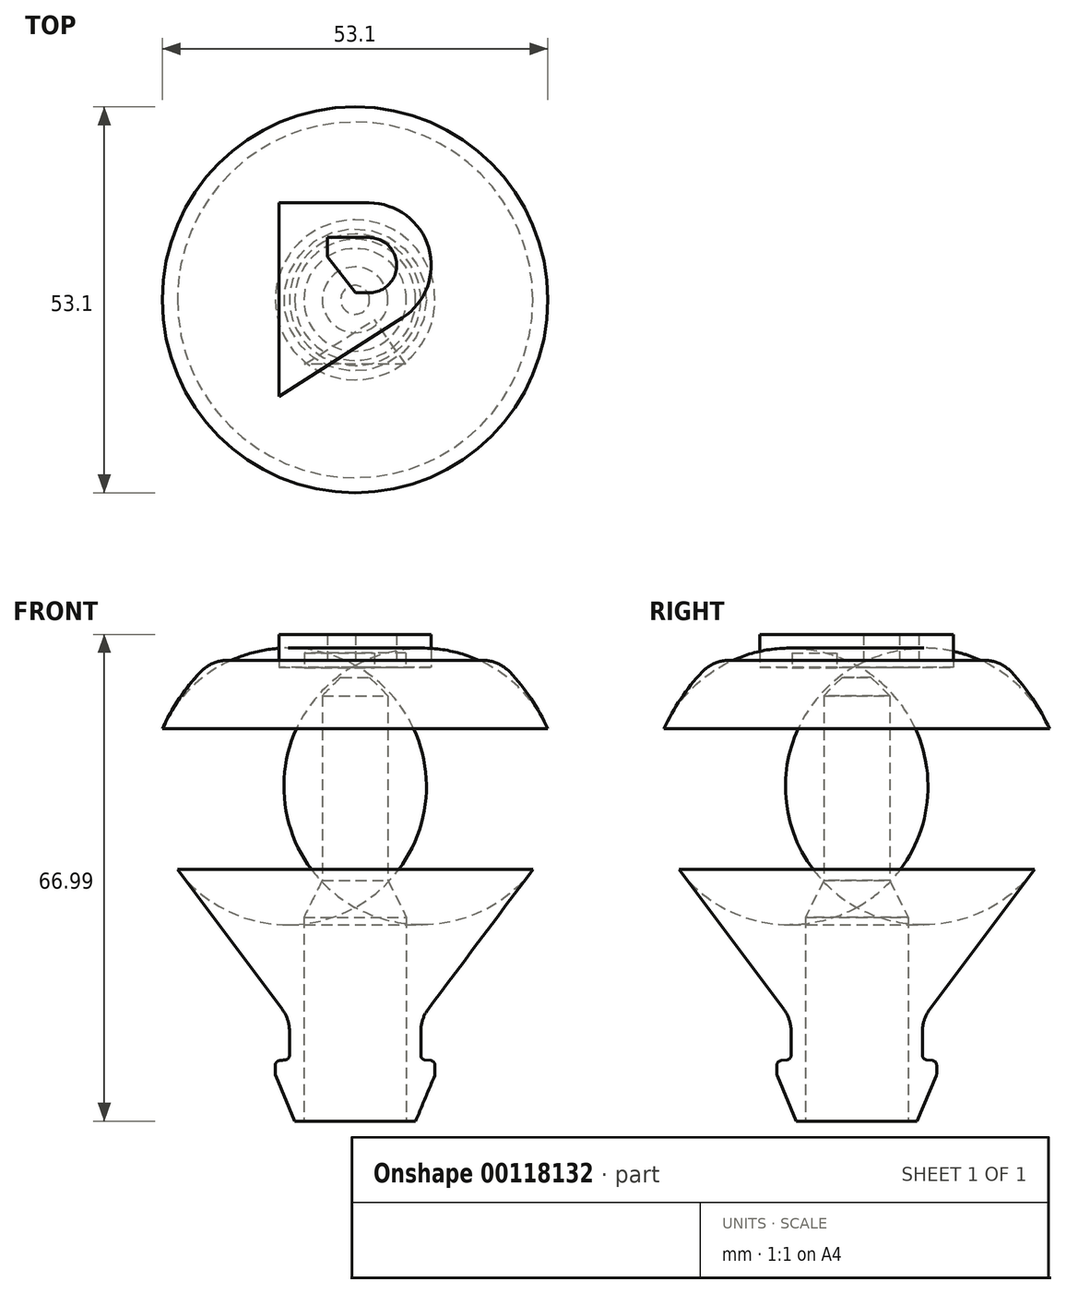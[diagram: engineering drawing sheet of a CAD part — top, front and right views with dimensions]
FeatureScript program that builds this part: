
annotation { "Feature Type Name" : "Feature", "Feature Type Description" : "" }
export const myFeature = defineFeature(function(context is Context, id is Id, definition is map)
    precondition{}
    {
        {
            var Q0;
            Q0=qCreatedBy(makeId("Front.planeOp"),FACE);
            var sketch = newSketch(context, id + "F0", { "sketchPlane" : qUnion([Q0])});
            skLineSegment(sketch, "E0", {"start": v(11, 6.35) * mm, "end": v(8.33, 0) * mm});
            skLineSegment(sketch, "E1", {"start": v(11, 6.35) * mm, "end": v(11, 8.26) * mm});
            skLineSegment(sketch, "E2", {"start": v(9.04, 8.5) * mm, "end": v(11, 8.26) * mm});
            skLineSegment(sketch, "E3", {"start": v(9.04, 8.5) * mm, "end": v(9.04, 14.05) * mm});
            skPoint(sketch, "E4", {"position": v(0, 61.09) * mm});
            skPoint(sketch, "E5", {"position": v(0, 75.49) * mm});
            skArc(sketch, "E6", {"start": v(29.2, 40.92) * mm, "mid": v(26.9, 53.2) * mm, "end": v(19.67, 63.41) * mm});
            skLineSegment(sketch, "E7", {"start": v(8.33, 0) * mm, "end": v(0, 0) * mm});
            skPoint(sketch, "E8", {"position": v(0, 71.03) * mm});
            skPoint(sketch, "E9", {"position": v(7.06, 0) * mm});
            skLineSegment(sketch, "E10", {"start": v(7.06, 0) * mm, "end": v(7.06, 28.07) * mm});
            skLineSegment(sketch, "E11", {"start": v(1.98, 61.09) * mm, "end": v(0, 61.09) * mm});
            skLineSegment(sketch, "E12", {"start": v(0, 61.09) * mm, "end": v(0, 63.41) * mm});
            skLineSegment(sketch, "E13", {"start": v(0, 63.41) * mm, "end": v(19.67, 63.41) * mm});
            skLineSegment(sketch, "E14", {"start": v(9.04, 14.05) * mm, "end": v(31.9, 44.53) * mm});
            skLineSegment(sketch, "E15", {"start": v(4.52, 58.55) * mm, "end": v(4.52, 33.15) * mm});
            skLineSegment(sketch, "E16", {"start": v(1.98, 61.09) * mm, "end": v(4.52, 58.55) * mm});
            skLineSegment(sketch, "E17", {"start": v(4.52, 33.15) * mm, "end": v(7.06, 28.07) * mm});
            skPoint(sketch, "E18.orphan", {"position": v(7.06, 61.09) * mm});
            skSolve(sketch);
        }
        {
            var Q0;
            {var subQ0=sQuery(id+"F0.wireOp",EDGE,"E0");Q0=makeQuery(id+"F0.imprint","IMPRINT",FACE,{"disambiguationData":[TD([[makeQuery(id+"F0.imprint","IMPRINT",EDGE,{"derivedFrom":subQ0}),-1.0]])]});}
            var Q1;
            Q1=sQuery(id+"F0.wireOp",EDGE,"E12");
            revolve(context, id + "F1", {"entities" : qUnion([Q0]), "axis" : qUnion([Q1]), "revolveType" : RevolveType.FULL});
        }
        {
            var Q0;
            Q0=makeQuery(id+"F1.opRevolve","SWEPT_EDGE",EDGE,{"disambiguationData":[OSD([sQuery(id+"F0.wireOp",EDGE,"E6"),sQuery(id+"F0.wireOp",EDGE,"E14")])]});
            fillet(context, id + "F2", {"entities" : qUnion([Q0]), "radius" : 19.05 * mm, "tangentPropagation" : true, "allowEdgeOverflow" : false});
        }
        {
            var Q0;
            Q0=makeQuery(id+"F1.opRevolve","SWEPT_EDGE",EDGE,{"disambiguationData":[OSD([sQuery(id+"F0.wireOp",EDGE,"E6"),sQuery(id+"F0.wireOp",EDGE,"E13")])]});
            fillet(context, id + "F3", {"entities" : qUnion([Q0]), "radius" : 5.08 * mm, "tangentPropagation" : true, "allowEdgeOverflow" : false});
        }
        {
            var Q0;
            Q0=makeQuery(id+"F1.opRevolve","SWEPT_EDGE",EDGE,{"disambiguationData":[OSD([sQuery(id+"F0.wireOp",EDGE,"E1"),sQuery(id+"F0.wireOp",EDGE,"E2")])]});
            var Q1;
            Q1=makeQuery(id+"F1.opRevolve","SWEPT_EDGE",EDGE,{"disambiguationData":[OSD([sQuery(id+"F0.wireOp",EDGE,"E0"),sQuery(id+"F0.wireOp",EDGE,"E1")])]});
            var Q2;
            Q2=makeQuery(id+"F1.opRevolve","SWEPT_EDGE",EDGE,{"disambiguationData":[OSD([sQuery(id+"F0.wireOp",EDGE,"E2"),sQuery(id+"F0.wireOp",EDGE,"E3")])]});
            fillet(context, id + "F4", {"entities" : qUnion([Q0, Q1, Q2]), "radius" : 0.64 * mm, "tangentPropagation" : true, "allowEdgeOverflow" : false});
        }
        {
            var Q0;
            Q0=makeQuery(id+"F1.opRevolve","SWEPT_EDGE",EDGE,{"disambiguationData":[OSD([sQuery(id+"F0.wireOp",EDGE,"E3"),sQuery(id+"F0.wireOp",EDGE,"E14")])]});
            fillet(context, id + "F5", {"entities" : qUnion([Q0]), "radius" : 5.08 * mm, "tangentPropagation" : true, "allowEdgeOverflow" : false});
        }
        {
            var Q0;
            Q0=qCreatedBy(makeId("Top.planeOp"),FACE);
            var sketch = newSketch(context, id + "F6", { "sketchPlane" : qUnion([Q0])});
            skLineSegment(sketch, "E19.bottom", {"start": v(1.27, 8.9) * mm, "end": v(-6.99, 8.89) * mm});
            skLineSegment(sketch, "E19.top", {"start": v(6.99, -8.9) * mm, "end": v(-6.99, -8.9) * mm});
            skLineSegment(sketch, "E19.right", {"start": v(-6.99, 8.9) * mm, "end": v(-6.99, -8.9) * mm});
            skPoint(sketch, "E19.middle", {"position": v(0, 0) * mm});
            skArc(sketch, "E20", {"start": v(4.35, -1.64) * mm, "mid": v(6.76, 4.78) * mm, "end": v(1.27, 8.89) * mm});
            skPoint(sketch, "E20.first.point", {"position": v(1.27, 8.9) * mm});
            skPoint(sketch, "E20.second.point", {"position": v(6.98, 3.17) * mm});
            skPoint(sketch, "E20.third.point.positionSnap0", {"position": v(6.99, 0) * mm});
            skLineSegment(sketch, "E21", {"start": v(-6.99, -8.9) * mm, "end": v(4.35, -1.64) * mm});
            skLineSegment(sketch, "E22", {"start": v(6.99, -8.9) * mm, "end": v(2.64, -2.73) * mm});
            skPoint(sketch, "E23.orphan", {"position": v(6.99, 8.9) * mm});
            skLineSegment(sketch, "E24", {"start": v(1.27, 8.9) * mm, "end": v(6.99, 8.9) * mm});
            skLineSegment(sketch, "E25", {"start": v(6.99, -8.9) * mm, "end": v(6.98, 8.9) * mm});
            skArc(sketch, "E26", {"start": v(1.25, 0.64) * mm, "mid": v(3.8, 3.16) * mm, "end": v(1.27, 5.71) * mm});
            skLineSegment(sketch, "E27", {"start": v(1.27, 5.72) * mm, "end": v(-2.54, 5.72) * mm});
            skLineSegment(sketch, "E28", {"start": v(-2.54, 5.72) * mm, "end": v(-2.54, 3.94) * mm});
            skLineSegment(sketch, "E29", {"start": v(1.3, 0.64) * mm, "end": v(0.03, 0.64) * mm});
            skLineSegment(sketch, "E30", {"start": v(0.03, 0.64) * mm, "end": v(-2.54, 3.94) * mm});
            skSolve(sketch);
        }
        {
            var Q0;
            {var subQ11=sQuery(id+"F6.wireOp",EDGE,"E19.bottom");Q0=makeQuery(id+"F6.imprint","IMPRINT",FACE,{"disambiguationData":[TD([[makeQuery(id+"F6.imprint","IMPRINT",EDGE,{"derivedFrom":subQ11}),1.0]])]});}
            extrude(context, id + "F7", {"entities" : qUnion([Q0]), "depth" : 65.4 * mm, "hasSecondDirection" : true, "secondDirectionOppositeDirection" : false, "secondDirectionDepth" : 62.4 * mm});
        }
        {
            var Q0;
            {var subQ0=sQuery(id+"F6.wireOp",EDGE,"E19.top");Q0=makeQuery(id+"F6.imprint","IMPRINT",FACE,{"disambiguationData":[TD([[makeQuery(id+"F6.imprint","IMPRINT",EDGE,{"derivedFrom":subQ0}),-1.0]])]});}
            extrude(context, id + "F8", {"entities" : qUnion([Q0]), "depth" : 64.43 * mm, "hasSecondDirection" : true, "secondDirectionOppositeDirection" : false, "secondDirectionDepth" : 62.38 * mm});
        }
        {
            var Q0;
            Q0=makeQuery(id+"F7.opExtrude","SWEPT_BODY",BODY,{"disambiguationData":[OSD([sQuery(id+"F6.wireOp",EDGE,"E19.bottom"),sQuery(id+"F6.wireOp",EDGE,"E19.right"),sQuery(id+"F6.wireOp",EDGE,"E20"),sQuery(id+"F6.wireOp",EDGE,"E21"),sQuery(id+"F6.wireOp",EDGE,"E26"),sQuery(id+"F6.wireOp",EDGE,"E27"),sQuery(id+"F6.wireOp",EDGE,"E28"),sQuery(id+"F6.wireOp",EDGE,"E29"),sQuery(id+"F6.wireOp",EDGE,"E30")])]});
            var Q1;
            Q1=qCreatedBy(makeId("Origin.pointOp"),VERTEX);
            transform(context, id + "F9", {"entities" : qUnion([Q0]), "transformType" : TransformType.SCALE_UNIFORMLY, "scale" : 1.5, "scalePoint" : qUnion([Q1]), "makeCopy" : false});
        }
        {
            var Q0;
            Q0=makeQuery(id+"F7.opExtrude","SWEPT_BODY",BODY,{"disambiguationData":[OSD([sQuery(id+"F6.wireOp",EDGE,"E19.bottom"),sQuery(id+"F6.wireOp",EDGE,"E19.right"),sQuery(id+"F6.wireOp",EDGE,"E20"),sQuery(id+"F6.wireOp",EDGE,"E21"),sQuery(id+"F6.wireOp",EDGE,"E26"),sQuery(id+"F6.wireOp",EDGE,"E27"),sQuery(id+"F6.wireOp",EDGE,"E28"),sQuery(id+"F6.wireOp",EDGE,"E29"),sQuery(id+"F6.wireOp",EDGE,"E30")])]});
            transform(context, id + "F10", {"entities" : qUnion([Q0]), "transformType" : TransformType.TRANSLATION_3D, "dx" : 0 * mm, "dy" : 0 * mm, "dz" : -31.12 * mm, "makeCopy" : false});
        }
    });
